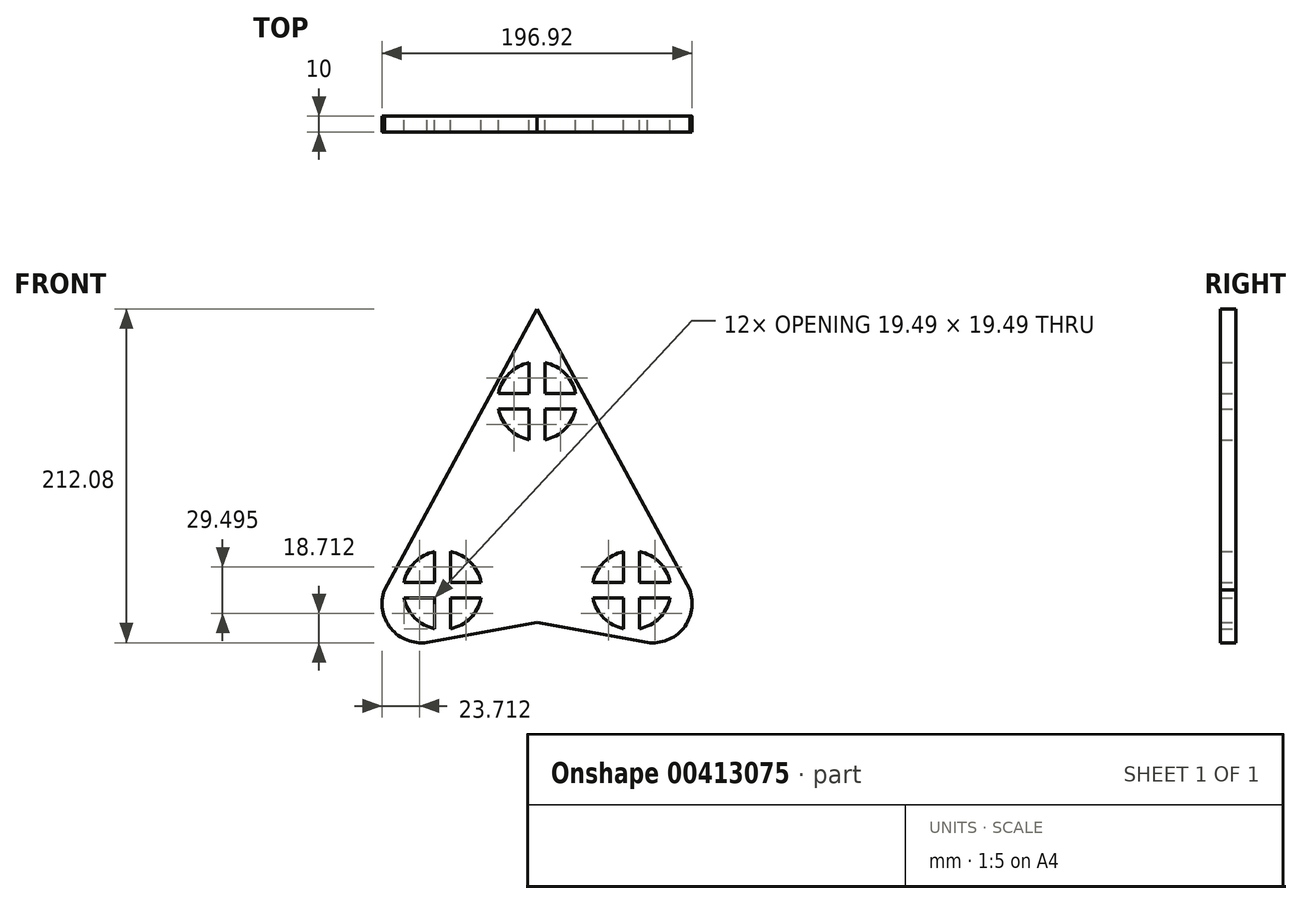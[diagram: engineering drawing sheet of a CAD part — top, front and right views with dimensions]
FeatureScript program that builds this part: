
annotation { "Feature Type Name" : "Feature", "Feature Type Description" : "" }
export const myFeature = defineFeature(function(context is Context, id is Id, definition is map)
    precondition{}
    {
        {
            var Q0;
            Q0=qCreatedBy(makeId("Front.planeOp"),FACE);
            var sketch = newSketch(context, id + "F0", { "sketchPlane" : qUnion([Q0])});
            skPoint(sketch, "E0", {"position": v(0, 60) * mm});
            skPoint(sketch, "E1", {"position": v(-60, -60) * mm});
            skPoint(sketch, "E2", {"position": v(60, -60) * mm});
            skCircle(sketch, "E3", {"center": v(0, 60) * mm, "radius": 25 * mm});
            skCircle(sketch, "E4", {"center": v(-60, -60) * mm, "radius": 25 * mm});
            skCircle(sketch, "E5", {"center": v(60, -60) * mm, "radius": 25 * mm});
            skPoint(sketch, "E6", {"position": v(0, -80.4) * mm});
            skPoint(sketch, "E7", {"position": v(0, 118.62) * mm});
            skPoint(sketch, "E8", {"position": v(-120, -102.4) * mm});
            skPoint(sketch, "E9", {"position": v(120, -102.4) * mm});
            skLineSegment(sketch, "E10", {"start": v(0, 118.62) * mm, "end": v(-96.98, -60) * mm});
            skLineSegment(sketch, "E11", {"start": v(0, 118.62) * mm, "end": v(96.98, -60) * mm});
            skLineSegment(sketch, "E12", {"start": v(0, -80.4) * mm, "end": v(70, -93.22) * mm});
            skLineSegment(sketch, "E13", {"start": v(0, -80.4) * mm, "end": v(-70, -93.22) * mm});
            skArc(sketch, "E14", {"start": v(-96.98, -60) * mm, "mid": v(-92.87, -84.23) * mm, "end": v(-70, -93.22) * mm});
            skArc(sketch, "E15", {"start": v(70, -93.22) * mm, "mid": v(92.87, -84.23) * mm, "end": v(96.98, -60) * mm});
            skLineSegment(sketch, "E16.bottom", {"start": v(24.5, 65) * mm, "end": v(5, 65) * mm});
            skLineSegment(sketch, "E16.top", {"start": v(24.5, 55) * mm, "end": v(5, 55) * mm});
            skLineSegment(sketch, "E17.left", {"start": v(5, 84.5) * mm, "end": v(5, 65) * mm});
            skLineSegment(sketch, "E17.right", {"start": v(-5, 84.5) * mm, "end": v(-5, 65) * mm});
            skLineSegment(sketch, "E18.left", {"start": v(-55, -35.5) * mm, "end": v(-55, -55) * mm});
            skLineSegment(sketch, "E18.right", {"start": v(-65, -35.5) * mm, "end": v(-65, -55) * mm});
            skLineSegment(sketch, "E19.bottom", {"start": v(-35.5, -55) * mm, "end": v(-55, -55) * mm});
            skLineSegment(sketch, "E19.top", {"start": v(-35.5, -65) * mm, "end": v(-55, -65) * mm});
            skLineSegment(sketch, "E20.left", {"start": v(65, -35.5) * mm, "end": v(65, -55) * mm});
            skLineSegment(sketch, "E20.right", {"start": v(55, -35.5) * mm, "end": v(55, -55) * mm});
            skLineSegment(sketch, "E21.bottom", {"start": v(35.5, -55) * mm, "end": v(55, -55) * mm});
            skLineSegment(sketch, "E21.top", {"start": v(35.5, -65) * mm, "end": v(55, -65) * mm});
            skLineSegment(sketch, "E22.trimOffspring", {"start": v(-55, -65) * mm, "end": v(-55, -84.5) * mm});
            skLineSegment(sketch, "E23.trimOffspring", {"start": v(-65, -65) * mm, "end": v(-65, -84.5) * mm});
            skLineSegment(sketch, "E24.trimOffspring", {"start": v(-65, -55) * mm, "end": v(-84.5, -55) * mm});
            skLineSegment(sketch, "E25.trimOffspring", {"start": v(-65, -65) * mm, "end": v(-84.5, -65) * mm});
            skLineSegment(sketch, "E26.trimOffspring", {"start": v(55, -65) * mm, "end": v(55, -84.5) * mm});
            skLineSegment(sketch, "E27.trimOffspring", {"start": v(65, -55) * mm, "end": v(84.5, -55) * mm});
            skLineSegment(sketch, "E28.trimOffspring", {"start": v(65, -65) * mm, "end": v(65, -84.5) * mm});
            skLineSegment(sketch, "E29.trimOffspring", {"start": v(65, -65) * mm, "end": v(84.5, -65) * mm});
            skLineSegment(sketch, "E30.trimOffspring", {"start": v(-5, 65) * mm, "end": v(-24.5, 65) * mm});
            skLineSegment(sketch, "E31.trimOffspring", {"start": v(-5, 55) * mm, "end": v(-5, 35.5) * mm});
            skLineSegment(sketch, "E32.trimOffspring", {"start": v(5, 55) * mm, "end": v(5, 35.5) * mm});
            skLineSegment(sketch, "E33.trimOffspring", {"start": v(-5, 55) * mm, "end": v(-24.5, 55) * mm});
            skSolve(sketch);
        }
        {
            var Q0;
            Q0=makeQuery(id+"F0.imprint","IMPRINT",FACE,{"disambiguationData":[TD([[makeQuery(id+"F0.imprint","IMPRINT",EDGE,{"derivedFrom":sQuery(id+"F0.wireOp",EDGE,"E10")}),1.0]])]});
            extrude(context, id + "F1", {"entities" : qUnion([Q0]), "depth" : 10 * mm});
        }
        {
            var Q0;
            {var subQ3=sQuery(id+"F0.wireOp",EDGE,"E18.left");Q0=makeQuery(id+"F0.imprint","IMPRINT",FACE,{"disambiguationData":[TD([[makeQuery(id+"F0.imprint","IMPRINT",EDGE,{"derivedFrom":subQ3}),-1.0]])]});}
            var Q1;
            {var subQ5=sQuery(id+"F0.wireOp",EDGE,"E20.left");Q1=makeQuery(id+"F0.imprint","IMPRINT",FACE,{"disambiguationData":[TD([[makeQuery(id+"F0.imprint","IMPRINT",EDGE,{"derivedFrom":subQ5}),-1.0]])]});}
            var Q2;
            {var subQ4=sQuery(id+"F0.wireOp",EDGE,"E16.bottom");Q2=makeQuery(id+"F0.imprint","IMPRINT",FACE,{"disambiguationData":[TD([[makeQuery(id+"F0.imprint","IMPRINT",EDGE,{"derivedFrom":subQ4}),1.0]])]});}
            extrude(context, id + "F2", {"entities" : qUnion([Q0, Q1, Q2]), "operationType" : NewBodyOperationType.ADD, "depth" : 10 * mm});
        }
    });
